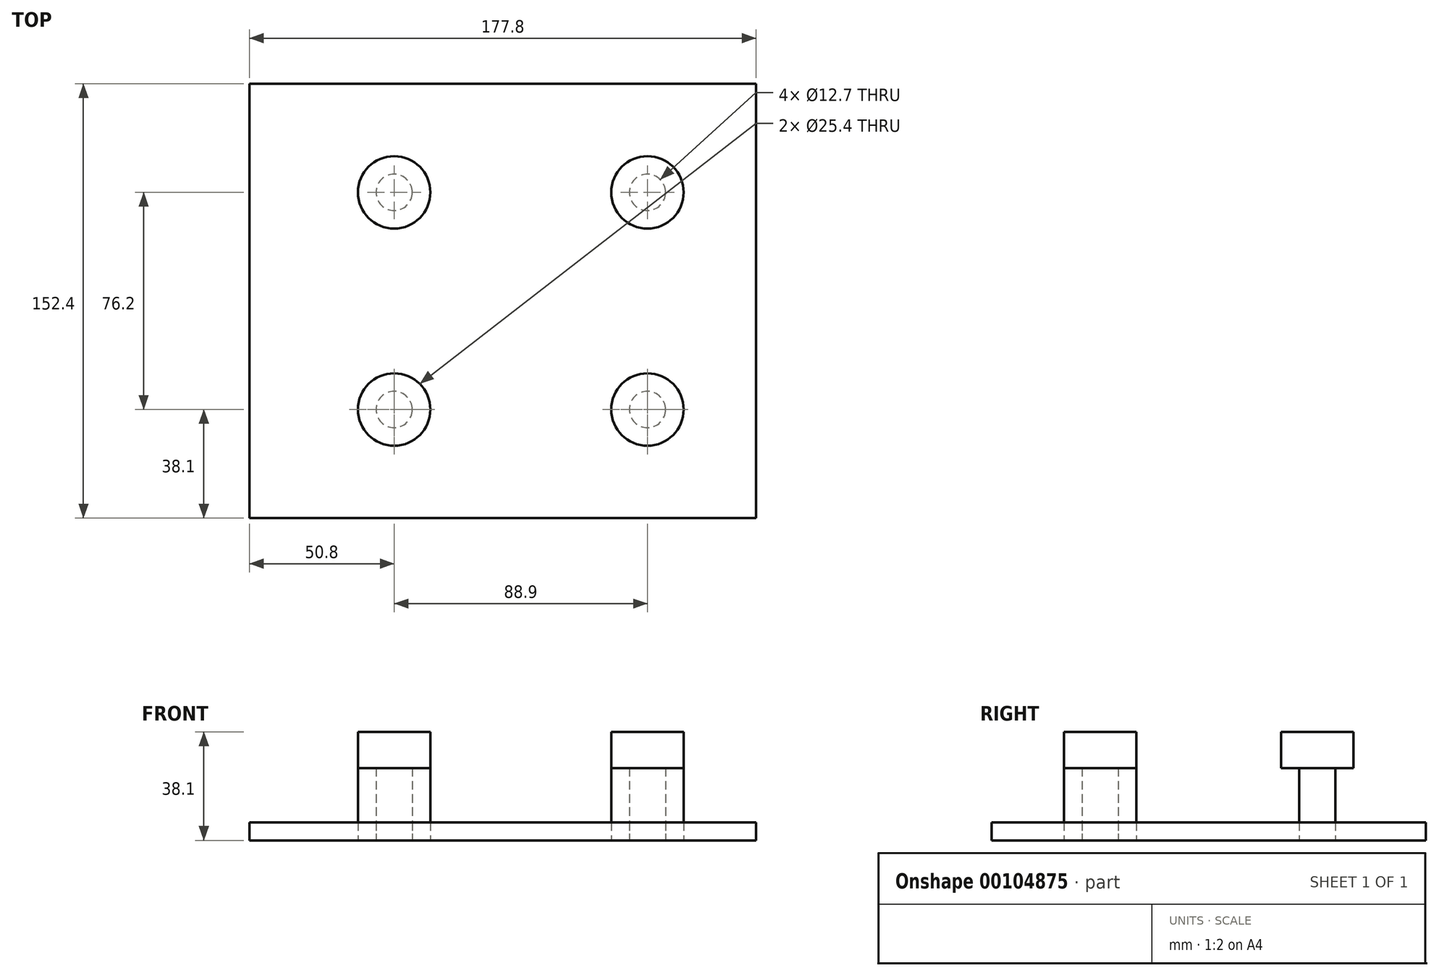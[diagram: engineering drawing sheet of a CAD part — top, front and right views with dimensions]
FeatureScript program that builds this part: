
annotation { "Feature Type Name" : "Feature", "Feature Type Description" : "" }
export const myFeature = defineFeature(function(context is Context, id is Id, definition is map)
    precondition{}
    {
        {
            var Q0;
            Q0=qCreatedBy(makeId("Top.planeOp"),FACE);
            var sketch = newSketch(context, id + "F0", { "sketchPlane" : qUnion([Q0])});
            skPoint(sketch, "E0.middle", {"position": v(0, 0) * mm});
            skCircle(sketch, "E1", {"center": v(63.5, 38.1) * mm, "radius": 6.35 * mm});
            skCircle(sketch, "E2", {"center": v(63.5, 38.1) * mm, "radius": 12.7 * mm});
            skCircle(sketch, "E3", {"center": v(-25.4, 38.1) * mm, "radius": 6.35 * mm});
            skCircle(sketch, "E4", {"center": v(-25.4, 38.1) * mm, "radius": 12.7 * mm});
            skPoint(sketch, "E5", {"position": v(-76.2, 0) * mm});
            skPoint(sketch, "E6", {"position": v(101.6, 0) * mm});
            skLineSegment(sketch, "E7", {"start": v(-76.2, 76.2) * mm, "end": v(-76.2, -76.2) * mm});
            skLineSegment(sketch, "E8.bottom", {"start": v(-76.2, 76.2) * mm, "end": v(101.6, 76.2) * mm});
            skLineSegment(sketch, "E8.top", {"start": v(-76.2, -76.2) * mm, "end": v(101.6, -76.2) * mm});
            skLineSegment(sketch, "E8.right", {"start": v(101.6, 76.2) * mm, "end": v(101.6, -76.2) * mm});
            skCircle(sketch, "E9.MirrorC", {"center": v(63.5, -38.1) * mm, "radius": 6.35 * mm});
            skCircle(sketch, "E10.MirrorC", {"center": v(63.5, -38.1) * mm, "radius": 12.7 * mm});
            skCircle(sketch, "E11.MirrorC", {"center": v(-25.4, -38.1) * mm, "radius": 6.35 * mm});
            skCircle(sketch, "E12.MirrorC", {"center": v(-25.4, -38.1) * mm, "radius": 12.7 * mm});
            skSolve(sketch);
        }
        {
            var Q0;
            Q0=makeQuery(id+"F0.imprint","IMPRINT",FACE,{"disambiguationData":[TD([[makeQuery(id+"F0.imprint","IMPRINT",EDGE,{"derivedFrom":sQuery(id+"F0.wireOp",EDGE,"E3")}),-1.0]])]});
            var Q1;
            Q1=makeQuery(id+"F0.imprint","IMPRINT",FACE,{"disambiguationData":[TD([[makeQuery(id+"F0.imprint","IMPRINT",EDGE,{"derivedFrom":sQuery(id+"F0.wireOp",EDGE,"E3")}),1.0]])]});
            var Q2;
            Q2=makeQuery(id+"F0.imprint","IMPRINT",FACE,{"disambiguationData":[TD([[makeQuery(id+"F0.imprint","IMPRINT",EDGE,{"derivedFrom":sQuery(id+"F0.wireOp",EDGE,"E1")}),1.0]])]});
            var Q3;
            Q3=makeQuery(id+"F0.imprint","IMPRINT",FACE,{"disambiguationData":[TD([[makeQuery(id+"F0.imprint","IMPRINT",EDGE,{"derivedFrom":sQuery(id+"F0.wireOp",EDGE,"E1")}),-1.0]])]});
            var Q4;
            Q4=makeQuery(id+"F0.imprint","IMPRINT",FACE,{"disambiguationData":[TD([[makeQuery(id+"F0.imprint","IMPRINT",EDGE,{"derivedFrom":sQuery(id+"F0.wireOp",EDGE,"E11.MirrorC")}),1.0]])]});
            var Q5;
            Q5=makeQuery(id+"F0.imprint","IMPRINT",FACE,{"disambiguationData":[TD([[makeQuery(id+"F0.imprint","IMPRINT",EDGE,{"derivedFrom":sQuery(id+"F0.wireOp",EDGE,"E11.MirrorC")}),-1.0]])]});
            var Q6;
            Q6=makeQuery(id+"F0.imprint","IMPRINT",FACE,{"disambiguationData":[TD([[makeQuery(id+"F0.imprint","IMPRINT",EDGE,{"derivedFrom":sQuery(id+"F0.wireOp",EDGE,"E9.MirrorC")}),-1.0]])]});
            var Q7;
            Q7=makeQuery(id+"F0.imprint","IMPRINT",FACE,{"disambiguationData":[TD([[makeQuery(id+"F0.imprint","IMPRINT",EDGE,{"derivedFrom":sQuery(id+"F0.wireOp",EDGE,"E9.MirrorC")}),1.0]])]});
            extrude(context, id + "F1", {"entities" : qUnion([Q0, Q1, Q2, Q3, Q4, Q5, Q6, Q7]), "depth" : 38.1 * mm, "hasSecondDirection" : true, "secondDirectionOppositeDirection" : false, "secondDirectionDepth" : 25.4 * mm});
        }
        {
            var Q0;
            Q0=makeQuery(id+"F0.imprint","IMPRINT",FACE,{"disambiguationData":[TD([[makeQuery(id+"F0.imprint","IMPRINT",EDGE,{"derivedFrom":sQuery(id+"F0.wireOp",EDGE,"E1")}),1.0]])]});
            var Q1;
            Q1=makeQuery(id+"F0.imprint","IMPRINT",FACE,{"disambiguationData":[TD([[makeQuery(id+"F0.imprint","IMPRINT",EDGE,{"derivedFrom":sQuery(id+"F0.wireOp",EDGE,"E3")}),1.0]])]});
            var Q2;
            Q2=makeQuery(id+"F0.imprint","IMPRINT",FACE,{"disambiguationData":[TD([[makeQuery(id+"F0.imprint","IMPRINT",EDGE,{"derivedFrom":sQuery(id+"F0.wireOp",EDGE,"E11.MirrorC")}),-1.0]])]});
            var Q3;
            Q3=makeQuery(id+"F0.imprint","IMPRINT",FACE,{"disambiguationData":[TD([[makeQuery(id+"F0.imprint","IMPRINT",EDGE,{"derivedFrom":sQuery(id+"F0.wireOp",EDGE,"E9.MirrorC")}),-1.0]])]});
            extrude(context, id + "F2", {"entities" : qUnion([Q0, Q1, Q2, Q3]), "depth" : 25.4 * mm});
        }
        {
            var Q0;
            Q0=makeQuery(id+"F0.imprint","IMPRINT",FACE,{"disambiguationData":[TD([[makeQuery(id+"F0.imprint","IMPRINT",EDGE,{"derivedFrom":sQuery(id+"F0.wireOp",EDGE,"E2")}),-1.0]])]});
            var Q1;
            Q1=makeQuery(id+"F0.imprint","IMPRINT",FACE,{"disambiguationData":[TD([[makeQuery(id+"F0.imprint","IMPRINT",EDGE,{"derivedFrom":sQuery(id+"F0.wireOp",EDGE,"E1")}),-1.0]])]});
            var Q2;
            Q2=makeQuery(id+"F0.imprint","IMPRINT",FACE,{"disambiguationData":[TD([[makeQuery(id+"F0.imprint","IMPRINT",EDGE,{"derivedFrom":sQuery(id+"F0.wireOp",EDGE,"E3")}),-1.0]])]});
            var Q3;
            Q3=makeQuery(id+"F0.imprint","IMPRINT",FACE,{"disambiguationData":[TD([[makeQuery(id+"F0.imprint","IMPRINT",EDGE,{"derivedFrom":sQuery(id+"F0.wireOp",EDGE,"E11.MirrorC")}),1.0]])]});
            var Q4;
            Q4=makeQuery(id+"F0.imprint","IMPRINT",FACE,{"disambiguationData":[TD([[makeQuery(id+"F0.imprint","IMPRINT",EDGE,{"derivedFrom":sQuery(id+"F0.wireOp",EDGE,"E9.MirrorC")}),1.0]])]});
            extrude(context, id + "F3", {"entities" : qUnion([Q0, Q1, Q2, Q3, Q4]), "depth" : 6.35 * mm});
        }
    });
